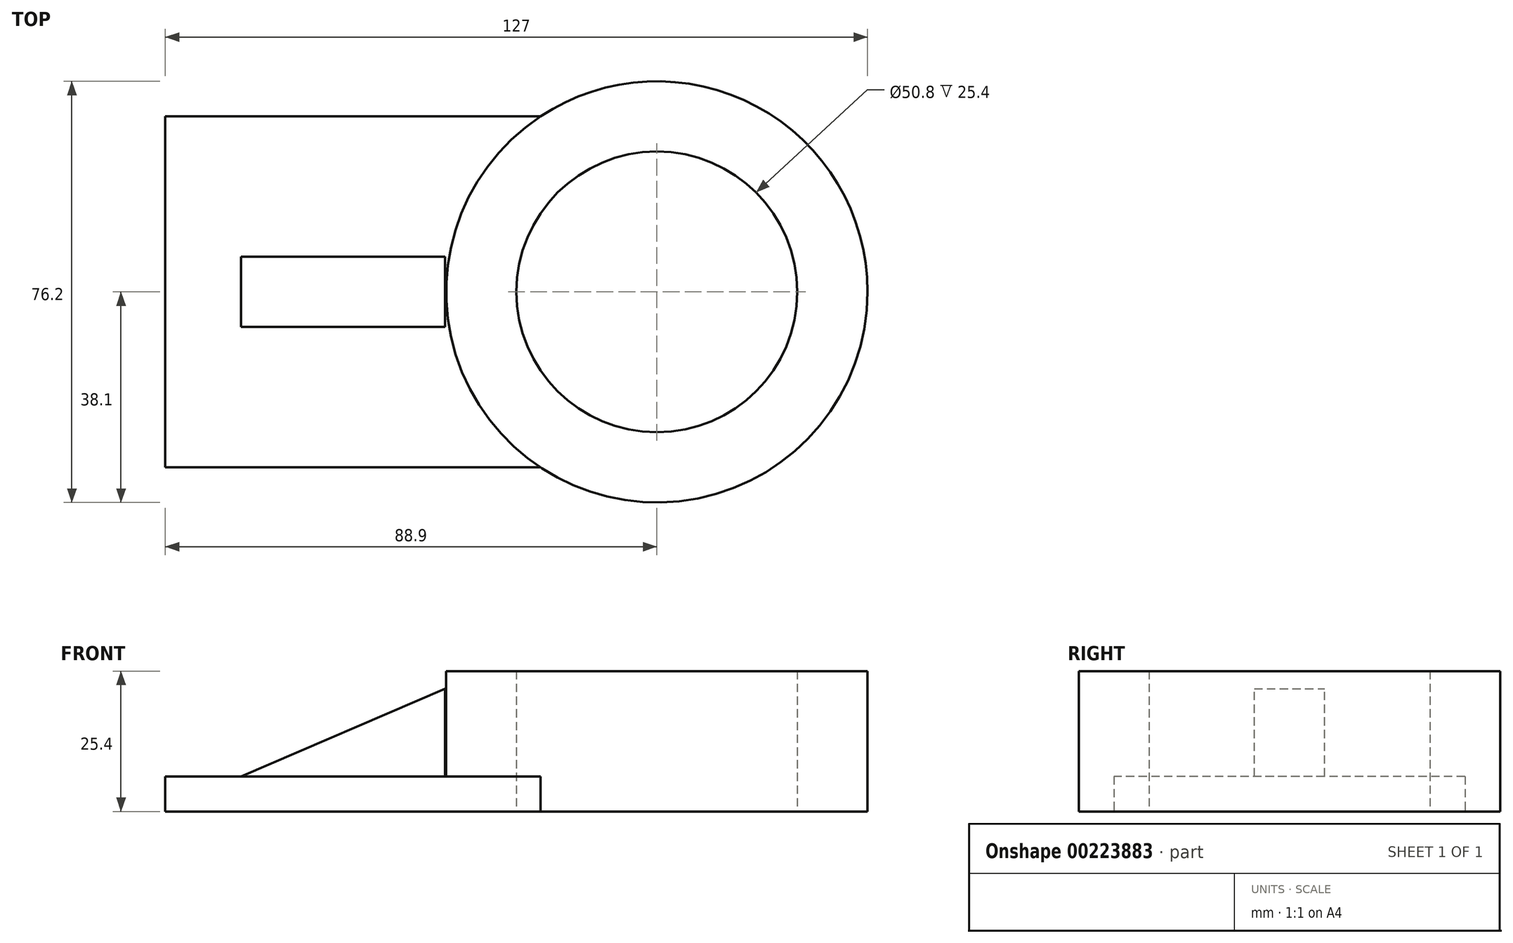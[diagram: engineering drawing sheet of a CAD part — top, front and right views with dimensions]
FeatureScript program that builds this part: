
annotation { "Feature Type Name" : "Feature", "Feature Type Description" : "" }
export const myFeature = defineFeature(function(context is Context, id is Id, definition is map)
    precondition{}
    {
        {
            var Q0;
            Q0=qCreatedBy(makeId("Top.planeOp"),FACE);
            var sketch = newSketch(context, id + "F0", { "sketchPlane" : qUnion([Q0])});
            skCircle(sketch, "E0", {"center": v(0, 0) * mm, "radius": 38.1 * mm});
            skCircle(sketch, "E1", {"center": v(0, 0) * mm, "radius": 25.4 * mm});
            skLineSegment(sketch, "E2.bottom", {"start": v(-88.9, 31.75) * mm, "end": v(-21.06, 31.75) * mm});
            skLineSegment(sketch, "E2.top", {"start": v(-88.9, -31.75) * mm, "end": v(-21.06, -31.75) * mm});
            skLineSegment(sketch, "E2.left", {"start": v(-88.9, 31.75) * mm, "end": v(-88.9, -31.75) * mm});
            skPoint(sketch, "E2.middle", {"position": v(-38.1, 0) * mm});
            skPoint(sketch, "E3.orphan", {"position": v(12.7, -31.75) * mm});
            skPoint(sketch, "E4.orphan", {"position": v(12.7, 31.75) * mm});
            skSolve(sketch);
        }
        {
            var Q0;
            {var subQ0=sQuery(id+"F0.wireOp",EDGE,"E2.bottom");Q0=makeQuery(id+"F0.imprint","IMPRINT",FACE,{"disambiguationData":[TD([[makeQuery(id+"F0.imprint","IMPRINT",EDGE,{"derivedFrom":subQ0}),-1.0]])]});}
            extrude(context, id + "F1", {"entities" : qUnion([Q0]), "depth" : 6.35 * mm});
        }
        {
            var Q0;
            Q0=makeQuery(id+"F0.imprint","IMPRINT",FACE,{"disambiguationData":[TD([[makeQuery(id+"F0.imprint","IMPRINT",EDGE,{"derivedFrom":sQuery(id+"F0.wireOp",EDGE,"E1")}),-1.0]])]});
            extrude(context, id + "F2", {"entities" : qUnion([Q0]), "operationType" : NewBodyOperationType.ADD, "depth" : 25.4 * mm});
        }
        {
            var Q0;
            Q0=qCreatedBy(makeId("Front.planeOp"),FACE);
            var sketch = newSketch(context, id + "F3", { "sketchPlane" : qUnion([Q0])});
            skLineSegment(sketch, "E5", {"start": v(-38.29, 3.13) * mm, "end": v(-38.29, 22.18) * mm});
            skLineSegment(sketch, "E6", {"start": v(-38.29, 3.13) * mm, "end": v(-82.74, 3.13) * mm});
            skLineSegment(sketch, "E7", {"start": v(-82.74, 3.13) * mm, "end": v(-38.29, 22.18) * mm});
            skSolve(sketch);
        }
        {
            var Q0;
            Q0 = qSketchRegion(id + "F3", true);
            extrude(context, id + "F4", {"entities" : qUnion([Q0]), "operationType" : NewBodyOperationType.ADD, "depth" : 6.35 * mm, "hasSecondDirection" : true, "secondDirectionOppositeDirection" : true, "secondDirectionDepth" : 6.35 * mm});
        }
    });
